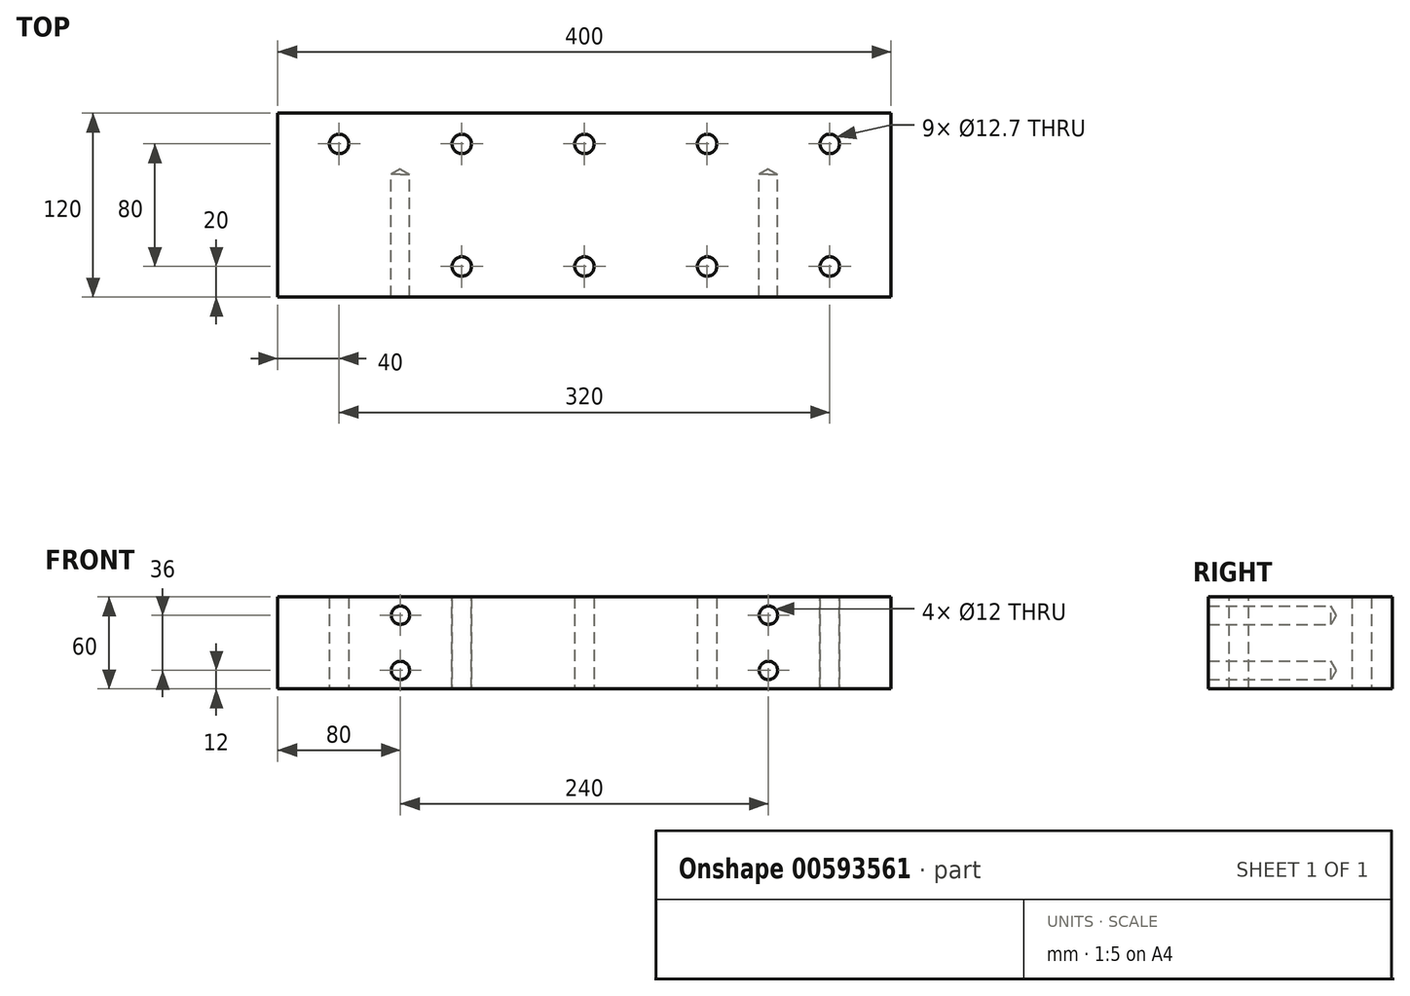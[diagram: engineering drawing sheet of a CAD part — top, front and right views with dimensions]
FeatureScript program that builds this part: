
annotation { "Feature Type Name" : "Feature", "Feature Type Description" : "" }
export const myFeature = defineFeature(function(context is Context, id is Id, definition is map)
    precondition{}
    {
        {
            var Q0;
            Q0=qCreatedBy(makeId("Top.planeOp"),FACE);
            var sketch = newSketch(context, id + "F0", { "sketchPlane" : qUnion([Q0])});
            skLineSegment(sketch, "E0.bottom", {"start": v(-200, 120) * mm, "end": v(200, 120) * mm});
            skLineSegment(sketch, "E0.top", {"start": v(-200, 0) * mm, "end": v(200, 0) * mm});
            skLineSegment(sketch, "E0.left", {"start": v(-200, 120) * mm, "end": v(-200, 0) * mm});
            skLineSegment(sketch, "E0.right", {"start": v(200, 120) * mm, "end": v(200, 0) * mm});
            skCircle(sketch, "E1.MirrorC", {"center": v(160, 20) * mm, "radius": 12.7 * mm});
            skCircle(sketch, "E2.MirrorC", {"center": v(80, 20) * mm, "radius": 12.7 * mm});
            skCircle(sketch, "E3.MirrorC", {"center": v(0, 20) * mm, "radius": 6.35 * mm});
            skCircle(sketch, "E4.MirrorC", {"center": v(-80, 20) * mm, "radius": 12.7 * mm});
            skCircle(sketch, "E5.MirrorC", {"center": v(-80, 20) * mm, "radius": 6.35 * mm});
            skCircle(sketch, "E6.MirrorC", {"center": v(0, 20) * mm, "radius": 12.7 * mm});
            skCircle(sketch, "E7.MirrorC", {"center": v(160, 20) * mm, "radius": 6.35 * mm});
            skCircle(sketch, "E8.MirrorC", {"center": v(80, 20) * mm, "radius": 6.35 * mm});
            skCircle(sketch, "E9.MirrorC", {"center": v(160, 100) * mm, "radius": 6.35 * mm});
            skCircle(sketch, "E10.MirrorC", {"center": v(160, 100) * mm, "radius": 12.7 * mm});
            skCircle(sketch, "E11.MirrorC", {"center": v(-160, 100) * mm, "radius": 6.35 * mm});
            skCircle(sketch, "E12.MirrorC", {"center": v(80, 100) * mm, "radius": 12.7 * mm});
            skCircle(sketch, "E13.MirrorC", {"center": v(80, 100) * mm, "radius": 6.35 * mm});
            skCircle(sketch, "E14.MirrorC", {"center": v(0, 100) * mm, "radius": 6.35 * mm});
            skCircle(sketch, "E15.MirrorC", {"center": v(-80, 100) * mm, "radius": 6.35 * mm});
            skCircle(sketch, "E16.MirrorC", {"center": v(0, 100) * mm, "radius": 12.7 * mm});
            skCircle(sketch, "E17.MirrorC", {"center": v(-80, 100) * mm, "radius": 12.7 * mm});
            skCircle(sketch, "E18.MirrorC", {"center": v(-160, 100) * mm, "radius": 12.7 * mm});
            skSolve(sketch);
        }
        {
            var Q0;
            Q0=makeQuery(id+"F0.imprint","IMPRINT",FACE,{"disambiguationData":[TD([[makeQuery(id+"F0.imprint","IMPRINT",EDGE,{"derivedFrom":sQuery(id+"F0.wireOp",EDGE,"E0.bottom")}),-1.0]])]});
            var Q1;
            Q1=makeQuery(id+"F0.imprint","IMPRINT",FACE,{"disambiguationData":[TD([[makeQuery(id+"F0.imprint","IMPRINT",EDGE,{"derivedFrom":sQuery(id+"F0.wireOp",EDGE,"E18.MirrorC")}),1.0]])]});
            var Q2;
            Q2=makeQuery(id+"F0.imprint","IMPRINT",FACE,{"disambiguationData":[TD([[makeQuery(id+"F0.imprint","IMPRINT",EDGE,{"derivedFrom":sQuery(id+"F0.wireOp",EDGE,"E11.MirrorC")}),1.0]])]});
            var Q3;
            Q3=makeQuery(id+"F0.imprint","IMPRINT",FACE,{"disambiguationData":[TD([[makeQuery(id+"F0.imprint","IMPRINT",EDGE,{"derivedFrom":sQuery(id+"F0.wireOp",EDGE,"E15.MirrorC")}),-1.0]])]});
            var Q4;
            Q4=makeQuery(id+"F0.imprint","IMPRINT",FACE,{"disambiguationData":[TD([[makeQuery(id+"F0.imprint","IMPRINT",EDGE,{"derivedFrom":sQuery(id+"F0.wireOp",EDGE,"E15.MirrorC")}),1.0]])]});
            var Q5;
            Q5=makeQuery(id+"F0.imprint","IMPRINT",FACE,{"disambiguationData":[TD([[makeQuery(id+"F0.imprint","IMPRINT",EDGE,{"derivedFrom":sQuery(id+"F0.wireOp",EDGE,"E14.MirrorC")}),-1.0]])]});
            var Q6;
            Q6=makeQuery(id+"F0.imprint","IMPRINT",FACE,{"disambiguationData":[TD([[makeQuery(id+"F0.imprint","IMPRINT",EDGE,{"derivedFrom":sQuery(id+"F0.wireOp",EDGE,"E14.MirrorC")}),1.0]])]});
            var Q7;
            Q7=makeQuery(id+"F0.imprint","IMPRINT",FACE,{"disambiguationData":[TD([[makeQuery(id+"F0.imprint","IMPRINT",EDGE,{"derivedFrom":sQuery(id+"F0.wireOp",EDGE,"E13.MirrorC")}),1.0]])]});
            var Q8;
            Q8=makeQuery(id+"F0.imprint","IMPRINT",FACE,{"disambiguationData":[TD([[makeQuery(id+"F0.imprint","IMPRINT",EDGE,{"derivedFrom":sQuery(id+"F0.wireOp",EDGE,"E12.MirrorC")}),1.0]])]});
            var Q9;
            Q9=makeQuery(id+"F0.imprint","IMPRINT",FACE,{"disambiguationData":[TD([[makeQuery(id+"F0.imprint","IMPRINT",EDGE,{"derivedFrom":sQuery(id+"F0.wireOp",EDGE,"E9.MirrorC")}),1.0]])]});
            var Q10;
            Q10=makeQuery(id+"F0.imprint","IMPRINT",FACE,{"disambiguationData":[TD([[makeQuery(id+"F0.imprint","IMPRINT",EDGE,{"derivedFrom":sQuery(id+"F0.wireOp",EDGE,"E9.MirrorC")}),-1.0]])]});
            var Q11;
            Q11=makeQuery(id+"F0.imprint","IMPRINT",FACE,{"disambiguationData":[TD([[makeQuery(id+"F0.imprint","IMPRINT",EDGE,{"derivedFrom":sQuery(id+"F0.wireOp",EDGE,"E8.MirrorC")}),-1.0]])]});
            var Q12;
            Q12=makeQuery(id+"F0.imprint","IMPRINT",FACE,{"disambiguationData":[TD([[makeQuery(id+"F0.imprint","IMPRINT",EDGE,{"derivedFrom":sQuery(id+"F0.wireOp",EDGE,"E8.MirrorC")}),1.0]])]});
            var Q13;
            Q13=makeQuery(id+"F0.imprint","IMPRINT",FACE,{"disambiguationData":[TD([[makeQuery(id+"F0.imprint","IMPRINT",EDGE,{"derivedFrom":sQuery(id+"F0.wireOp",EDGE,"E7.MirrorC")}),-1.0]])]});
            var Q14;
            Q14=makeQuery(id+"F0.imprint","IMPRINT",FACE,{"disambiguationData":[TD([[makeQuery(id+"F0.imprint","IMPRINT",EDGE,{"derivedFrom":sQuery(id+"F0.wireOp",EDGE,"E1.MirrorC")}),-1.0]])]});
            var Q15;
            Q15=makeQuery(id+"F0.imprint","IMPRINT",FACE,{"disambiguationData":[TD([[makeQuery(id+"F0.imprint","IMPRINT",EDGE,{"derivedFrom":sQuery(id+"F0.wireOp",EDGE,"E3.MirrorC")}),-1.0]])]});
            var Q16;
            Q16=makeQuery(id+"F0.imprint","IMPRINT",FACE,{"disambiguationData":[TD([[makeQuery(id+"F0.imprint","IMPRINT",EDGE,{"derivedFrom":sQuery(id+"F0.wireOp",EDGE,"E3.MirrorC")}),1.0]])]});
            var Q17;
            Q17=makeQuery(id+"F0.imprint","IMPRINT",FACE,{"disambiguationData":[TD([[makeQuery(id+"F0.imprint","IMPRINT",EDGE,{"derivedFrom":sQuery(id+"F0.wireOp",EDGE,"E5.MirrorC")}),-1.0]])]});
            var Q18;
            Q18=makeQuery(id+"F0.imprint","IMPRINT",FACE,{"disambiguationData":[TD([[makeQuery(id+"F0.imprint","IMPRINT",EDGE,{"derivedFrom":sQuery(id+"F0.wireOp",EDGE,"E4.MirrorC")}),-1.0]])]});
            extrude(context, id + "F1", {"entities" : qUnion([Q0, Q1, Q2, Q3, Q4, Q5, Q6, Q7, Q8, Q9, Q10, Q11, Q12, Q13, Q14, Q15, Q16, Q17, Q18]), "oppositeDirection" : true, "depth" : 60 * mm, "offsetDistance" : 25 * mm});
        }
        {
            var Q0;
            Q0=qCreatedBy(makeId("Front.planeOp"),FACE);
            var sketch = newSketch(context, id + "F2", { "sketchPlane" : qUnion([Q0])});
            skLineSegment(sketch, "E19.bottom", {"start": v(-200, 0) * mm, "end": v(200, 0) * mm});
            skLineSegment(sketch, "E19.top", {"start": v(-200, -60) * mm, "end": v(200, -60) * mm});
            skLineSegment(sketch, "E19.left", {"start": v(-200, 0) * mm, "end": v(-200, -60) * mm});
            skLineSegment(sketch, "E19.right", {"start": v(200, 0) * mm, "end": v(200, -60) * mm});
            skPoint(sketch, "E20", {"position": v(-120, -12) * mm});
            skPoint(sketch, "E21", {"position": v(-120, -48) * mm});
            skPoint(sketch, "E22", {"position": v(120, -48) * mm});
            skPoint(sketch, "E23", {"position": v(120, -12) * mm});
            skSolve(sketch);
        }
        {
            var Q0;
            Q0=sQuery(id+"F2.wireOp",VERTEX,"E20");
            var Q1;
            Q1=sQuery(id+"F2.wireOp",VERTEX,"E21");
            var Q2;
            Q2=sQuery(id+"F2.wireOp",VERTEX,"E22");
            var Q3;
            Q3=sQuery(id+"F2.wireOp",VERTEX,"E23");
            var Q4;
            Q4=makeQuery(id+"F1.opExtrude","SWEPT_BODY",BODY,{"disambiguationData":[OSD([sQuery(id+"F0.wireOp",EDGE,"E0.bottom"),sQuery(id+"F0.wireOp",EDGE,"E0.top"),sQuery(id+"F0.wireOp",EDGE,"E0.left"),sQuery(id+"F0.wireOp",EDGE,"E0.right"),sQuery(id+"F0.wireOp",EDGE,"E4.MirrorC"),sQuery(id+"F0.wireOp",EDGE,"E1.MirrorC"),sQuery(id+"F0.wireOp",EDGE,"E6.MirrorC"),sQuery(id+"F0.wireOp",EDGE,"E2.MirrorC"),sQuery(id+"F0.wireOp",EDGE,"E18.MirrorC"),sQuery(id+"F0.wireOp",EDGE,"E10.MirrorC"),sQuery(id+"F0.wireOp",EDGE,"E12.MirrorC"),sQuery(id+"F0.wireOp",EDGE,"E16.MirrorC"),sQuery(id+"F0.wireOp",EDGE,"E17.MirrorC")])]});
            hole(context, id + "F3", {"style" : HoleStyle.SIMPLE, "endStyle" : HoleEndStyle.BLIND, "holeDiameter" : 12 * mm, "majorDiameter" : 5 * mm, "holeDepth" : 80 * mm, "isTappedThrough" : true, "tappedDepth" : 20 * mm, "tapClearance" : 3, "startFromSketch" : true, "locations" : qUnion([Q0, Q1, Q2, Q3]), "scope" : qUnion([Q4])});
        }
        {
            var Q0;
            Q0=sQuery(id+"F0.wireOp",VERTEX,"E4.MirrorC.center");
            var Q1;
            Q1=sQuery(id+"F0.wireOp",VERTEX,"E15.MirrorC.center");
            var Q2;
            Q2=sQuery(id+"F0.wireOp",VERTEX,"E11.MirrorC.center");
            var Q3;
            Q3=sQuery(id+"F0.wireOp",VERTEX,"E14.MirrorC.center");
            var Q4;
            Q4=sQuery(id+"F0.wireOp",VERTEX,"E3.MirrorC.center");
            var Q5;
            Q5=sQuery(id+"F0.wireOp",VERTEX,"E2.MirrorC.center");
            var Q6;
            Q6=sQuery(id+"F0.wireOp",VERTEX,"E12.MirrorC.center");
            var Q7;
            Q7=sQuery(id+"F0.wireOp",VERTEX,"E9.MirrorC.center");
            var Q8;
            Q8=sQuery(id+"F0.wireOp",VERTEX,"E1.MirrorC.center");
            var Q9;
            Q9=makeQuery(id+"F1.opExtrude","SWEPT_BODY",BODY,{"disambiguationData":[OSD([sQuery(id+"F0.wireOp",EDGE,"E0.bottom"),sQuery(id+"F0.wireOp",EDGE,"E0.top"),sQuery(id+"F0.wireOp",EDGE,"E0.left"),sQuery(id+"F0.wireOp",EDGE,"E0.right")])]});
            hole(context, id + "F4", {"style" : HoleStyle.SIMPLE, "endStyle" : HoleEndStyle.THROUGH, "holeDiameter" : 12.7 * mm, "majorDiameter" : 5 * mm, "isTappedThrough" : true, "tappedDepth" : 20 * mm, "tapClearance" : 3, "locations" : qUnion([Q0, Q1, Q2, Q3, Q4, Q5, Q6, Q7, Q8]), "scope" : qUnion([Q9])});
        }
    });
